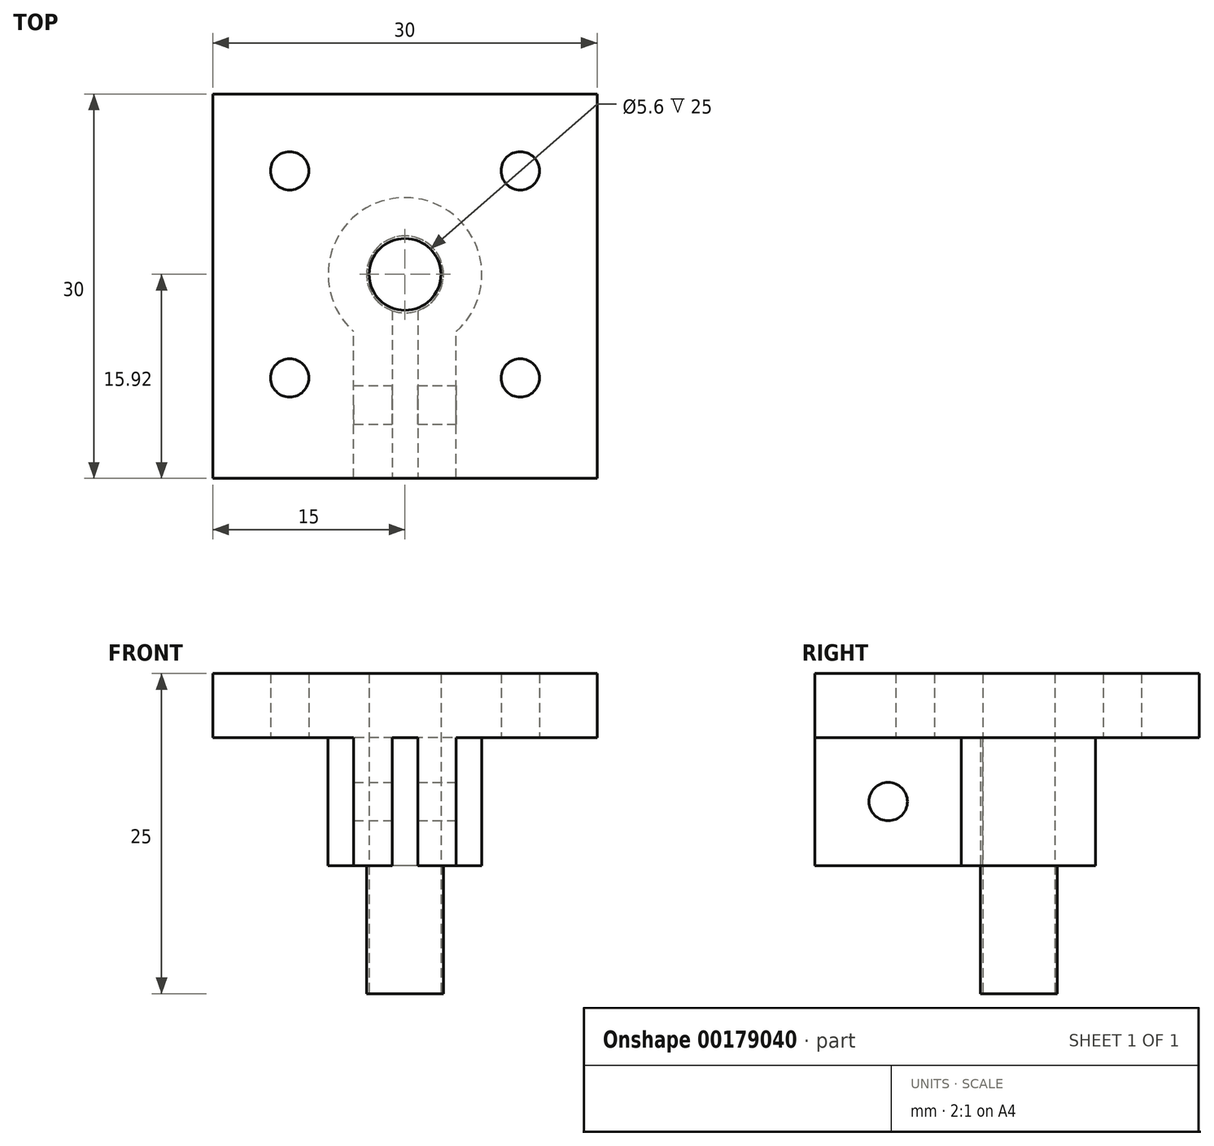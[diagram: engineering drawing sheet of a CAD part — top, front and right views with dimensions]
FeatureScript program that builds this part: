
annotation { "Feature Type Name" : "Feature", "Feature Type Description" : "" }
export const myFeature = defineFeature(function(context is Context, id is Id, definition is map)
    precondition{}
    {
        {
            var Q0;
            Q0=qCreatedBy(makeId("Top.planeOp"),FACE);
            var sketch = newSketch(context, id + "F0", { "sketchPlane" : qUnion([Q0])});
            skCircle(sketch, "E0", {"center": v(0, 0) * mm, "radius": 3 * mm});
            skCircle(sketch, "E1", {"center": v(0, 0) * mm, "radius": 2.8 * mm});
            skSolve(sketch);
        }
        {
            var Q0;
            Q0 = qSketchRegion(id + "F0", true);
            extrude(context, id + "F1", {"entities" : qUnion([Q0]), "depth" : 20 * mm});
        }
        {
            var Q0;
            Q0=qCreatedBy(makeId("Top.planeOp"),FACE);
            cPlane(context, id + "F2", {"entities" : qUnion([Q0]), "cplaneType" : CPlaneType.OFFSET, "offset" : 10 * mm, "width" : 150 * mm, "height" : 150 * mm});
        }
        {
            var Q0;
            Q0=qCreatedBy(id+"F2.planeOp",FACE);
            var sketch = newSketch(context, id + "F3", { "sketchPlane" : qUnion([Q0])});
            skCircle(sketch, "E2.0", {"center": v(0, 0) * mm, "radius": 3 * mm});
            skArc(sketch, "E3.0.0", {"start": v(1, -2.83) * mm, "mid": v(0, 3) * mm, "end": v(-1, -2.83) * mm});
            skArc(sketch, "E4", {"start": v(4, -4.47) * mm, "mid": v(0, 6) * mm, "end": v(-4, -4.47) * mm});
            skLineSegment(sketch, "E5", {"start": v(-1, -2.83) * mm, "end": v(-1, -5.92) * mm});
            skLineSegment(sketch, "E6.MirrorCS", {"start": v(1, -2.83) * mm, "end": v(1, -5.92) * mm});
            skLineSegment(sketch, "E7", {"start": v(-1, -5.92) * mm, "end": v(-1, -15.92) * mm});
            skLineSegment(sketch, "E8", {"start": v(-1, -15.92) * mm, "end": v(-4, -15.92) * mm});
            skLineSegment(sketch, "E9", {"start": v(-4, -15.92) * mm, "end": v(-4, -4.47) * mm});
            skLineSegment(sketch, "E10.MirrorCS", {"start": v(1, -5.92) * mm, "end": v(1, -15.92) * mm});
            skLineSegment(sketch, "E11.MirrorCS", {"start": v(1, -15.92) * mm, "end": v(4, -15.92) * mm});
            skLineSegment(sketch, "E12.MirrorCS", {"start": v(4, -15.92) * mm, "end": v(4, -4.47) * mm});
            skSolve(sketch);
        }
        {
            var Q0;
            Q0=makeQuery(id+"F3.imprint","IMPRINT",FACE,{"disambiguationData":[TD([[makeQuery(id+"F3.imprint","IMPRINT",EDGE,{"derivedFrom":sQuery(id+"F3.wireOp",EDGE,"E4")}),1.0]])]});
            extrude(context, id + "F4", {"entities" : qUnion([Q0]), "depth" : 10 * mm});
        }
        {
            var Q0;
            Q0=makeQuery(id+"F4.opExtrude","SWEPT_FACE",FACE,{"disambiguationData":[OSD([sQuery(id+"F3.wireOp",EDGE,"E12.MirrorCS")])]});
            var sketch = newSketch(context, id + "F5", { "sketchPlane" : qUnion([Q0])});
            skCircle(sketch, "E13", {"center": v(-10.2, 15) * mm, "radius": 1.5 * mm});
            skPoint(sketch, "E13.centerSnap0", {"position": v(-15.92, 15) * mm});
            skPoint(sketch, "E13.centerSnap1", {"position": v(-10.2, 20) * mm});
            skSolve(sketch);
        }
        {
            var Q0;
            Q0 = qSketchRegion(id + "F5", true);
            extrude(context, id + "F6", {"entities" : qUnion([Q0]), "operationType" : NewBodyOperationType.REMOVE, "endBound" : BoundingType.THROUGH_ALL, "oppositeDirection" : true, "depth" : 25 * mm});
        }
        {
            var Q0;
            Q0=makeQuery(id+"F4.opExtrude","CAP_FACE",FACE,{"disambiguationData":[OSD([sQuery(id+"F3.wireOp",EDGE,"E2.0"),sQuery(id+"F3.wireOp",EDGE,"E4"),sQuery(id+"F3.wireOp",EDGE,"E5"),sQuery(id+"F3.wireOp",EDGE,"E6.MirrorCS"),sQuery(id+"F3.wireOp",EDGE,"E7"),sQuery(id+"F3.wireOp",EDGE,"E8"),sQuery(id+"F3.wireOp",EDGE,"E9"),sQuery(id+"F3.wireOp",EDGE,"E10.MirrorCS"),sQuery(id+"F3.wireOp",EDGE,"E11.MirrorCS"),sQuery(id+"F3.wireOp",EDGE,"E12.MirrorCS")])],"isStart":false});
            var sketch = newSketch(context, id + "F7", { "sketchPlane" : qUnion([Q0])});
            skCircle(sketch, "E14.0", {"center": v(0, 0) * mm, "radius": 2.8 * mm});
            skLineSegment(sketch, "E15.bottom", {"start": v(-15, 14.08) * mm, "end": v(15, 14.08) * mm});
            skLineSegment(sketch, "E15.top", {"start": v(-15, -15.92) * mm, "end": v(15, -15.92) * mm});
            skLineSegment(sketch, "E15.left", {"start": v(-15, 14.08) * mm, "end": v(-15, -15.92) * mm});
            skLineSegment(sketch, "E15.right", {"start": v(15, 14.08) * mm, "end": v(15, -15.92) * mm});
            skCircle(sketch, "E16", {"center": v(-9, 8.08) * mm, "radius": 1.5 * mm});
            skCircle(sketch, "E17.MirrorC", {"center": v(9, 8.08) * mm, "radius": 1.5 * mm});
            skCircle(sketch, "E18.MirrorC", {"center": v(9, -8.08) * mm, "radius": 1.5 * mm});
            skCircle(sketch, "E19.MirrorC", {"center": v(-9, -8.08) * mm, "radius": 1.5 * mm});
            skSolve(sketch);
        }
        {
            var Q0;
            Q0 = qSketchRegion(id + "F7", true);
            extrude(context, id + "F8", {"entities" : qUnion([Q0]), "operationType" : NewBodyOperationType.ADD, "depth" : 5 * mm});
        }
    });
